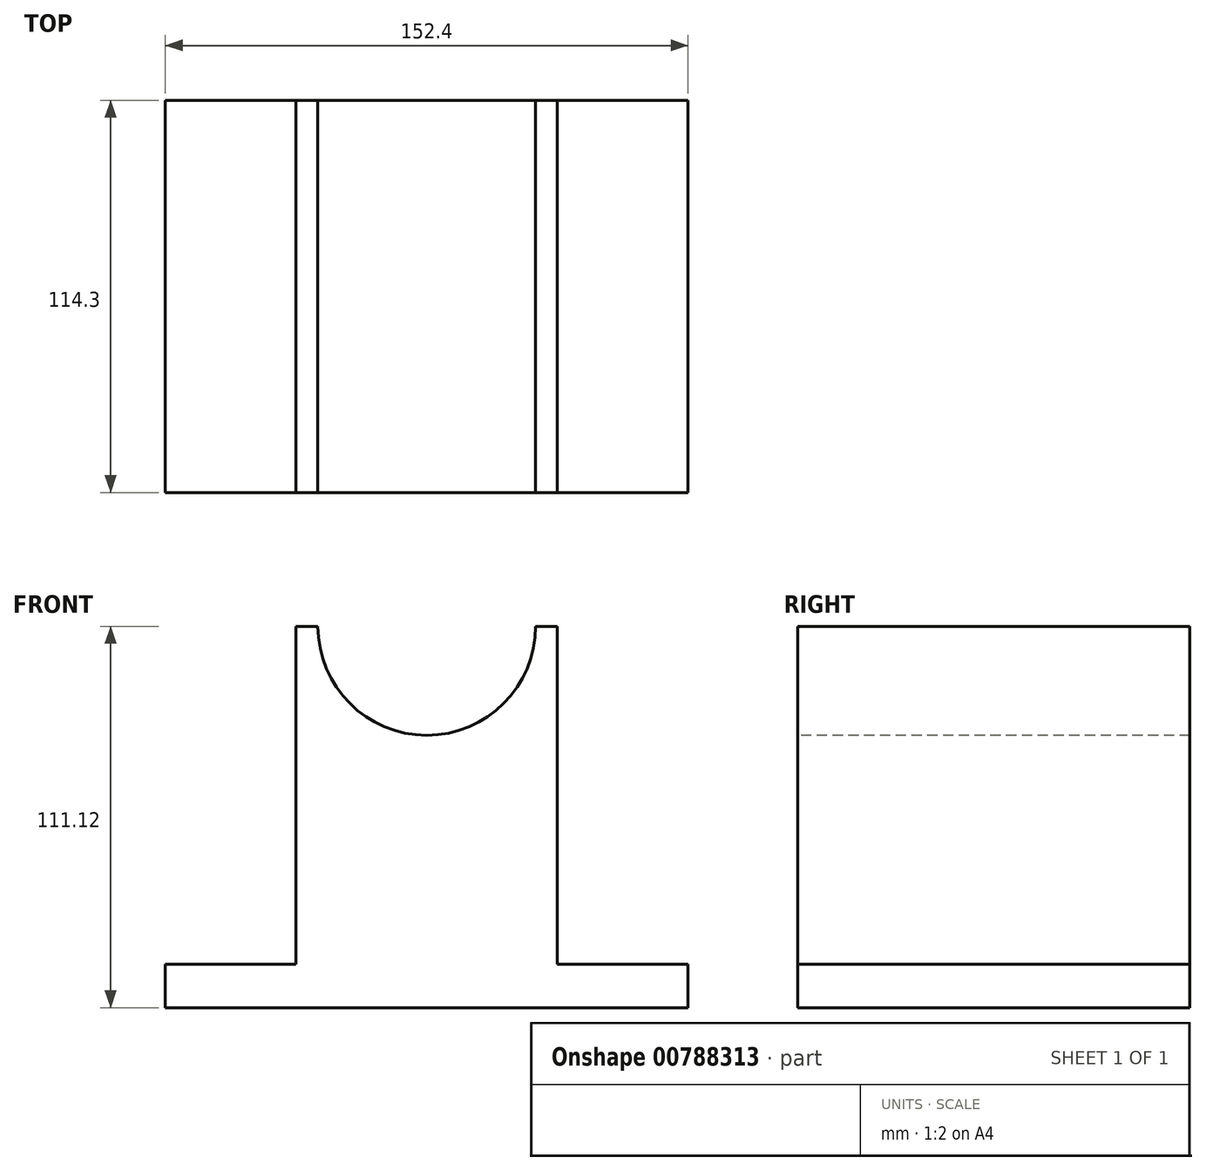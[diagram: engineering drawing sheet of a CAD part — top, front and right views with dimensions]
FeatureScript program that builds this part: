
annotation { "Feature Type Name" : "Feature", "Feature Type Description" : "" }
export const myFeature = defineFeature(function(context is Context, id is Id, definition is map)
    precondition{}
    {
        {
            var Q0;
            Q0=qCreatedBy(makeId("Front.planeOp"),FACE);
            var sketch = newSketch(context, id + "F0", { "sketchPlane" : qUnion([Q0])});
            skLineSegment(sketch, "E0", {"start": v(0, 0) * mm, "end": v(152.4, 0) * mm});
            skLineSegment(sketch, "E1", {"start": v(152.4, 0) * mm, "end": v(152.4, 12.7) * mm});
            skLineSegment(sketch, "E2", {"start": v(152.4, 12.7) * mm, "end": v(114.3, 12.7) * mm});
            skLineSegment(sketch, "E3", {"start": v(114.3, 12.7) * mm, "end": v(114.3, 111.12) * mm});
            skLineSegment(sketch, "E4", {"start": v(114.3, 111.12) * mm, "end": v(38.1, 111.12) * mm});
            skLineSegment(sketch, "E5", {"start": v(38.1, 111.12) * mm, "end": v(38.1, 12.7) * mm});
            skLineSegment(sketch, "E6", {"start": v(38.1, 12.7) * mm, "end": v(0, 12.7) * mm});
            skLineSegment(sketch, "E7", {"start": v(0, 12.7) * mm, "end": v(0, 0) * mm});
            skSolve(sketch);
        }
        {
            var Q0;
            Q0=makeQuery(id+"F0.imprint","IMPRINT",FACE,{"disambiguationData":[TD([[makeQuery(id+"F0.imprint","IMPRINT",EDGE,{"derivedFrom":sQuery(id+"F0.wireOp",EDGE,"E0")}),1.0]])]});
            extrude(context, id + "F1", {"entities" : qUnion([Q0]), "depth" : 114.3 * mm, "offsetDistance" : 25.4 * mm});
        }
        {
            var Q0;
            Q0=makeQuery(id+"F1.opExtrude","CAP_FACE",FACE,{"disambiguationData":[OSD([sQuery(id+"F0.wireOp",EDGE,"E0"),sQuery(id+"F0.wireOp",EDGE,"E1"),sQuery(id+"F0.wireOp",EDGE,"E2"),sQuery(id+"F0.wireOp",EDGE,"E3"),sQuery(id+"F0.wireOp",EDGE,"E4"),sQuery(id+"F0.wireOp",EDGE,"E5"),sQuery(id+"F0.wireOp",EDGE,"E6"),sQuery(id+"F0.wireOp",EDGE,"E7")])],"isStart":false});
            var sketch = newSketch(context, id + "F2", { "sketchPlane" : qUnion([Q0])});
            skLineSegment(sketch, "E8", {"start": v(38.1, 111.12) * mm, "end": v(44.45, 111.12) * mm});
            skLineSegment(sketch, "E9", {"start": v(114.3, 111.12) * mm, "end": v(107.95, 111.12) * mm});
            skArc(sketch, "E10", {"start": v(44.45, 111.12) * mm, "mid": v(76.2, 79.38) * mm, "end": v(107.95, 111.12) * mm});
            skSolve(sketch);
        }
        {
            var Q0;
            {var subQ0=sQuery(id+"F2.wireOp",EDGE,"E10");Q0=makeQuery(id+"F2.imprint","IMPRINT",FACE,{"disambiguationData":[TD([[makeQuery(id+"F2.imprint","IMPRINT",EDGE,{"derivedFrom":subQ0}),1.0]])]});}
            extrude(context, id + "F3", {"entities" : qUnion([Q0]), "operationType" : NewBodyOperationType.REMOVE, "endBound" : BoundingType.UP_TO_NEXT, "oppositeDirection" : true, "depth" : 25.4 * mm, "offsetDistance" : 25.4 * mm});
        }
    });
